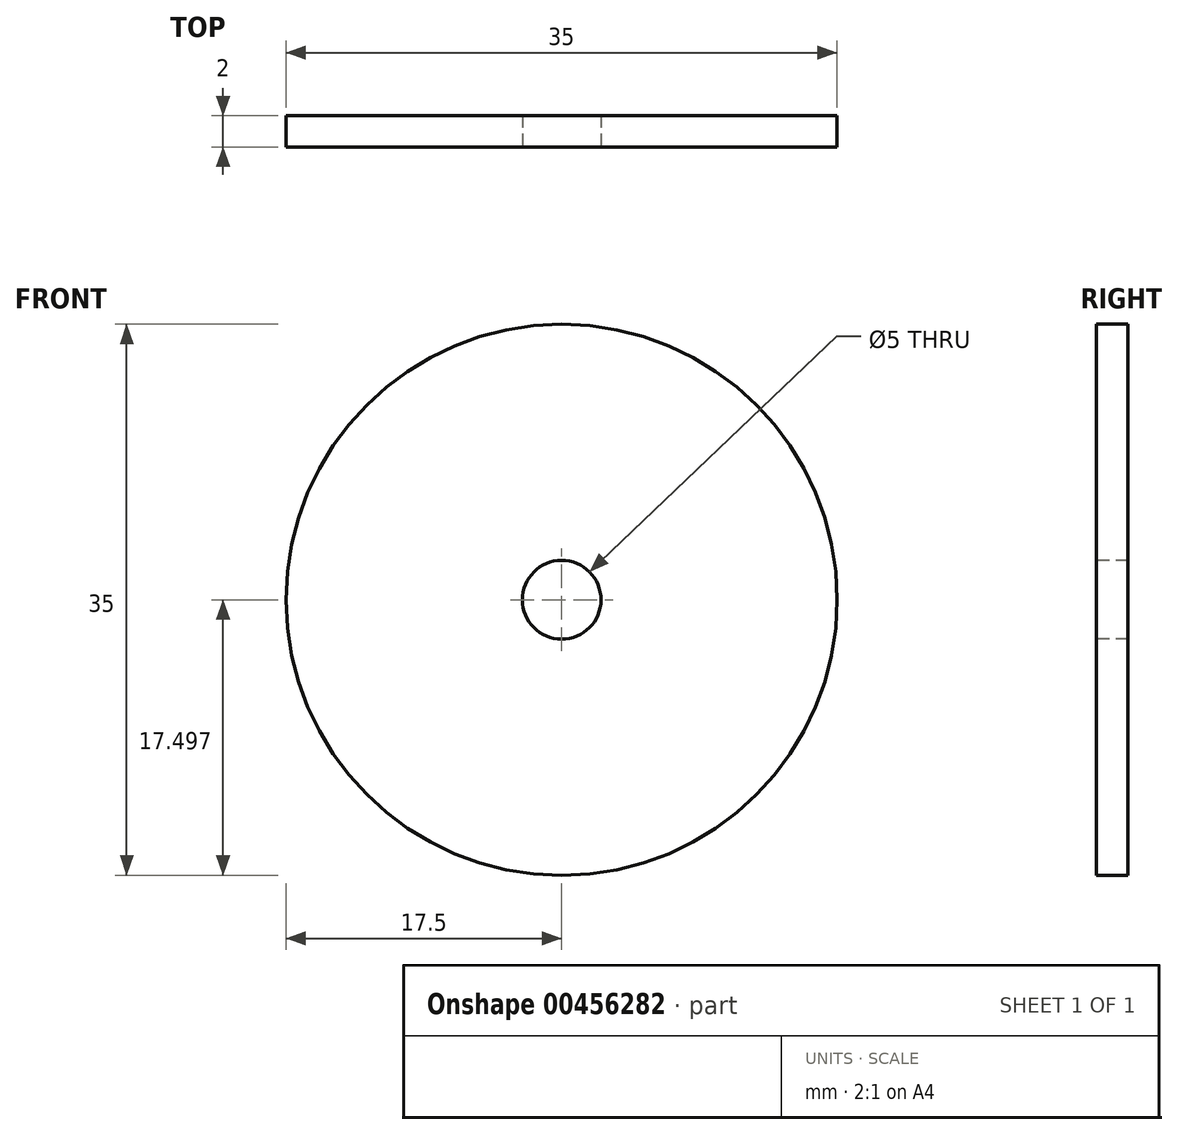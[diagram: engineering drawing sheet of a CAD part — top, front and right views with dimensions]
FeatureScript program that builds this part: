
annotation { "Feature Type Name" : "Feature", "Feature Type Description" : "" }
export const myFeature = defineFeature(function(context is Context, id is Id, definition is map)
    precondition{}
    {
        {
            var Q0;
            Q0=qCreatedBy(makeId("Front.planeOp"),FACE);
            var sketch = newSketch(context, id + "F0", { "sketchPlane" : qUnion([Q0])});
            skCircle(sketch, "E0", {"center": v(-15.67, 19.36) * mm, "radius": 17.5 * mm});
            skSolve(sketch);
        }
        {
            var Q0;
            Q0=qSketchRegion(id+"F0",true);
            extrude(context, id + "F1", {"entities" : qUnion([Q0]), "depth" : 2 * mm});
        }
        {
            var Q0;
            Q0=makeQuery(id+"F1.opExtrude","CAP_FACE",FACE,{"disambiguationData":[OSD([sQuery(id+"F0.wireOp",EDGE,"E0")])],"isStart":false});
            var sketch = newSketch(context, id + "F2", { "sketchPlane" : qUnion([Q0])});
            skCircle(sketch, "E1", {"center": v(-15.67, 19.36) * mm, "radius": 2.5 * mm});
            skSolve(sketch);
        }
        {
            var Q0;
            Q0=makeQuery(id+"F2.imprint","IMPRINT",FACE,{"disambiguationData":[TD([[makeQuery(id+"F2.imprint","IMPRINT",EDGE,{"derivedFrom":sQuery(id+"F2.wireOp",EDGE,"E1")}),1.0]])]});
            extrude(context, id + "F3", {"entities" : qUnion([Q0]), "operationType" : NewBodyOperationType.ADD, "depth" : 6 * mm});
        }
        {
            var Q0;
            Q0=makeQuery(id+"F1.opExtrude","CAP_FACE",FACE,{"disambiguationData":[OSD([sQuery(id+"F0.wireOp",EDGE,"E0")])],"isStart":true});
            var sketch = newSketch(context, id + "F4", { "sketchPlane" : qUnion([Q0])});
            skCircle(sketch, "E2", {"center": v(15.67, 19.36) * mm, "radius": 2.5 * mm});
            skSolve(sketch);
        }
        {
            var Q0;
            Q0=qSketchRegion(id+"F4",true);
            extrude(context, id + "F5", {"entities" : qUnion([Q0]), "operationType" : NewBodyOperationType.ADD, "depth" : 6 * mm});
        }
        {
            var Q0;
            Q0=makeQuery(id+"F3.opExtrude","CAP_FACE",FACE,{"disambiguationData":[OSD([sQuery(id+"F2.wireOp",EDGE,"E1")])],"isStart":false});
            extrude(context, id + "F6", {"entities" : qUnion([Q0]), "operationType" : NewBodyOperationType.REMOVE, "endBound" : BoundingType.THROUGH_ALL, "oppositeDirection" : true, "depth" : 25.4 * mm});
        }
    });
